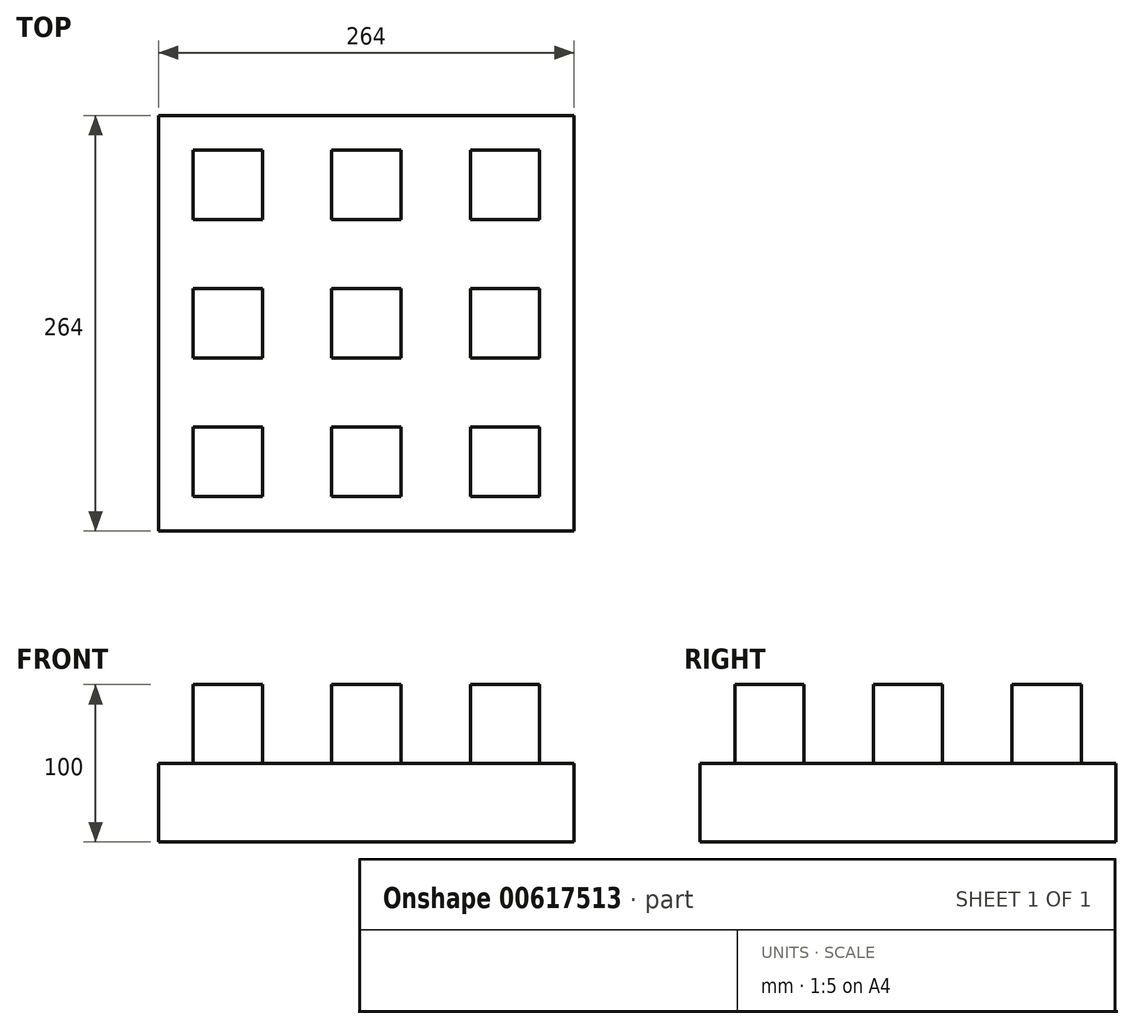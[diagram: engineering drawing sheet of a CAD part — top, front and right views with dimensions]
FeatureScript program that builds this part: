
annotation { "Feature Type Name" : "Feature", "Feature Type Description" : "" }
export const myFeature = defineFeature(function(context is Context, id is Id, definition is map)
    precondition{}
    {
        {
            var Q0;
            Q0=qCreatedBy(makeId("Top.planeOp"),FACE);
            var sketch = newSketch(context, id + "F0", { "sketchPlane" : qUnion([Q0])});
            skLineSegment(sketch, "E0.bottom", {"start": v(22, -22) * mm, "end": v(-22, -22) * mm});
            skLineSegment(sketch, "E0.top", {"start": v(22, 22) * mm, "end": v(-22, 22) * mm});
            skLineSegment(sketch, "E0.left", {"start": v(22, -22) * mm, "end": v(22, 22) * mm});
            skLineSegment(sketch, "E0.right", {"start": v(-22, -22) * mm, "end": v(-22, 22) * mm});
            skPoint(sketch, "E0.middle", {"position": v(0, 0) * mm});
            skLineSegment(sketch, "E1.bottom", {"start": v(-66, -22) * mm, "end": v(-110, -22) * mm});
            skLineSegment(sketch, "E1.top", {"start": v(-66, 22) * mm, "end": v(-110, 22) * mm});
            skLineSegment(sketch, "E1.left", {"start": v(-66, -22) * mm, "end": v(-66, 22) * mm});
            skLineSegment(sketch, "E1.right", {"start": v(-110, -22) * mm, "end": v(-110, 22) * mm});
            skPoint(sketch, "E1.middle", {"position": v(-88, 0) * mm});
            skPoint(sketch, "E1.middle.positionSnap0", {"position": v(-22, 0) * mm});
            skPoint(sketch, "E1.centerSnap0", {"position": v(-22, 0) * mm});
            skLineSegment(sketch, "E2.bottom", {"start": v(22, 66) * mm, "end": v(-22, 66) * mm});
            skLineSegment(sketch, "E2.top", {"start": v(22, 110) * mm, "end": v(-22, 110) * mm});
            skLineSegment(sketch, "E2.left", {"start": v(22, 66) * mm, "end": v(22, 110) * mm});
            skLineSegment(sketch, "E2.right", {"start": v(-22, 66) * mm, "end": v(-22, 110) * mm});
            skLineSegment(sketch, "E3.bottom", {"start": v(-66, 66) * mm, "end": v(-110, 66) * mm});
            skLineSegment(sketch, "E3.top", {"start": v(-66, 110) * mm, "end": v(-110, 110) * mm});
            skLineSegment(sketch, "E3.left", {"start": v(-66, 66) * mm, "end": v(-66, 110) * mm});
            skLineSegment(sketch, "E3.right", {"start": v(-110, 66) * mm, "end": v(-110, 110) * mm});
            skLineSegment(sketch, "E4.bottom", {"start": v(-132, 132) * mm, "end": v(132, 132) * mm});
            skLineSegment(sketch, "E4.top", {"start": v(-132, -132) * mm, "end": v(132, -132) * mm});
            skLineSegment(sketch, "E4.left", {"start": v(-132, 132) * mm, "end": v(-132, -132) * mm});
            skLineSegment(sketch, "E4.right", {"start": v(132, 132) * mm, "end": v(132, -132) * mm});
            skSolve(sketch);
        }
        {
            var Q0;
            Q0=makeQuery(id+"F0.imprint","IMPRINT",FACE,{"disambiguationData":[TD([[makeQuery(id+"F0.imprint","IMPRINT",EDGE,{"derivedFrom":sQuery(id+"F0.wireOp",EDGE,"E1.bottom")}),-1.0]])]});
            var Q1;
            Q1=makeQuery(id+"F0.imprint","IMPRINT",FACE,{"disambiguationData":[TD([[makeQuery(id+"F0.imprint","IMPRINT",EDGE,{"derivedFrom":sQuery(id+"F0.wireOp",EDGE,"E3.bottom")}),-1.0]])]});
            var Q2;
            Q2=makeQuery(id+"F0.imprint","IMPRINT",FACE,{"disambiguationData":[TD([[makeQuery(id+"F0.imprint","IMPRINT",EDGE,{"derivedFrom":sQuery(id+"F0.wireOp",EDGE,"E2.bottom")}),-1.0]])]});
            var Q3;
            Q3=makeQuery(id+"F0.imprint","IMPRINT",FACE,{"disambiguationData":[TD([[makeQuery(id+"F0.imprint","IMPRINT",EDGE,{"derivedFrom":sQuery(id+"F0.wireOp",EDGE,"E0.bottom")}),-1.0]])]});
            extrude(context, id + "F1", {"entities" : qUnion([Q0, Q1, Q2, Q3]), "depth" : 50 * mm, "offsetDistance" : 25 * mm});
        }
        {
            var Q0;
            Q0=makeQuery(id+"F1.opExtrude","SWEPT_BODY",BODY,{"disambiguationData":[OSD([sQuery(id+"F0.wireOp",EDGE,"E1.bottom"),sQuery(id+"F0.wireOp",EDGE,"E1.top"),sQuery(id+"F0.wireOp",EDGE,"E1.left"),sQuery(id+"F0.wireOp",EDGE,"E1.right")])]});
            var Q1;
            Q1=makeQuery(id+"F1.opExtrude","SWEPT_BODY",BODY,{"disambiguationData":[OSD([sQuery(id+"F0.wireOp",EDGE,"E3.bottom"),sQuery(id+"F0.wireOp",EDGE,"E3.top"),sQuery(id+"F0.wireOp",EDGE,"E3.left"),sQuery(id+"F0.wireOp",EDGE,"E3.right")])]});
            var Q2;
            Q2=qCreatedBy(makeId("Right.planeOp"),FACE);
            mirror(context, id + "F2", {"entities" : qUnion([Q0, Q1]), "mirrorPlane" : qUnion([Q2])});
        }
        {
            var Q0;
            Q0=makeQuery(id+"F1.opExtrude","SWEPT_BODY",BODY,{"disambiguationData":[OSD([sQuery(id+"F0.wireOp",EDGE,"E3.bottom"),sQuery(id+"F0.wireOp",EDGE,"E3.top"),sQuery(id+"F0.wireOp",EDGE,"E3.left"),sQuery(id+"F0.wireOp",EDGE,"E3.right")])]});
            var Q1;
            Q1=makeQuery(id+"F1.opExtrude","SWEPT_BODY",BODY,{"disambiguationData":[OSD([sQuery(id+"F0.wireOp",EDGE,"E2.bottom"),sQuery(id+"F0.wireOp",EDGE,"E2.top"),sQuery(id+"F0.wireOp",EDGE,"E2.left"),sQuery(id+"F0.wireOp",EDGE,"E2.right")])]});
            var Q2;
            Q2=makeQuery(id+"F2.opPattern","COPY",BODY,{"derivedFrom":makeQuery(id+"F1.opExtrude","SWEPT_BODY",BODY,{"disambiguationData":[OSD([sQuery(id+"F0.wireOp",EDGE,"E3.bottom"),sQuery(id+"F0.wireOp",EDGE,"E3.top"),sQuery(id+"F0.wireOp",EDGE,"E3.left"),sQuery(id+"F0.wireOp",EDGE,"E3.right")])]}),"instanceName":"1"});
            var Q3;
            Q3=qCreatedBy(makeId("Front.planeOp"),FACE);
            mirror(context, id + "F3", {"entities" : qUnion([Q0, Q1, Q2]), "mirrorPlane" : qUnion([Q3])});
        }
        {
            var Q0;
            Q0=makeQuery(id+"F0.imprint","IMPRINT",FACE,{"disambiguationData":[TD([[makeQuery(id+"F0.imprint","IMPRINT",EDGE,{"derivedFrom":sQuery(id+"F0.wireOp",EDGE,"E0.bottom")}),1.0]])]});
            var Q1;
            Q1=makeQuery(id+"F0.imprint","IMPRINT",FACE,{"disambiguationData":[TD([[makeQuery(id+"F0.imprint","IMPRINT",EDGE,{"derivedFrom":sQuery(id+"F0.wireOp",EDGE,"E1.bottom")}),-1.0]])]});
            var Q2;
            Q2=makeQuery(id+"F0.imprint","IMPRINT",FACE,{"disambiguationData":[TD([[makeQuery(id+"F0.imprint","IMPRINT",EDGE,{"derivedFrom":sQuery(id+"F0.wireOp",EDGE,"E0.bottom")}),-1.0]])]});
            var Q3;
            Q3=makeQuery(id+"F0.imprint","IMPRINT",FACE,{"disambiguationData":[TD([[makeQuery(id+"F0.imprint","IMPRINT",EDGE,{"derivedFrom":sQuery(id+"F0.wireOp",EDGE,"E3.bottom")}),-1.0]])]});
            var Q4;
            Q4=makeQuery(id+"F0.imprint","IMPRINT",FACE,{"disambiguationData":[TD([[makeQuery(id+"F0.imprint","IMPRINT",EDGE,{"derivedFrom":sQuery(id+"F0.wireOp",EDGE,"E2.bottom")}),-1.0]])]});
            extrude(context, id + "F4", {"entities" : qUnion([Q0, Q1, Q2, Q3, Q4]), "oppositeDirection" : true, "depth" : 50 * mm, "offsetDistance" : 25 * mm});
        }
    });
